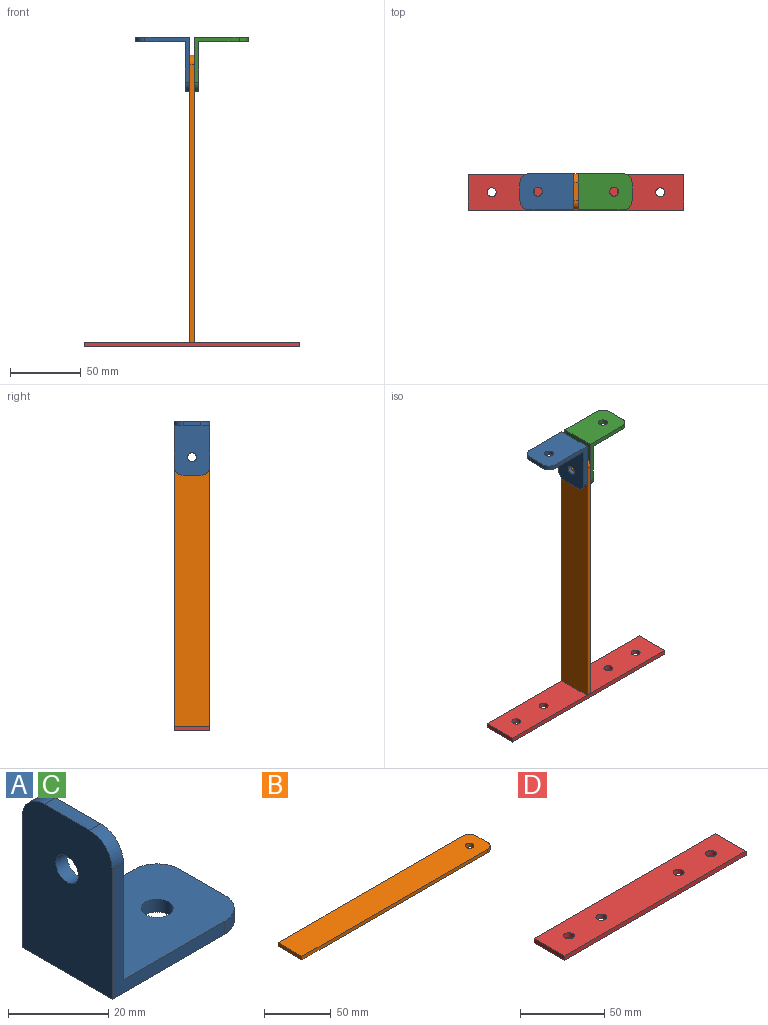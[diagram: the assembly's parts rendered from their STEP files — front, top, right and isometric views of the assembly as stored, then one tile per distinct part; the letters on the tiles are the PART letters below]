
ASSEMBLY  parts=4 mates=3
PART A: 14 faces, bbox 38.1x25.4x38.1 mm
  f0: plane 31.75x31.75mm, normal (0,-1,0), area 191.5mm2, adj f3,f5,f6,f7,f8,f11
  f1: plane 12.7x3.18mm, normal (1,0,0), area 40.3mm2, adj f5,f7,f8,f9
  f2: plane 31.75x31.75mm, normal (0,1,0), area 191.5mm2, adj f3,f5,f6,f7,f9,f10
  f3: plane 38.1x25.4mm, normal (-1,0,0), area 918.8mm2, adj f0,f2,f4,f5,f10,f11,f12
  f4: plane 12.7x3.18mm, normal (0,0,1), area 40.3mm2, adj f3,f6,f10,f11
  f5: plane 38.1x25.4mm, normal (0,0,-1), area 918.8mm2, adj f0,f1,f2,f3,f8,f9,f13
  f6: plane 34.93x25.4mm, normal (1,0,0), area 838.1mm2, adj f0,f2,f4,f7,f10,f11,f12
  f7: plane 34.93x25.4mm, normal (0,0,1), area 838.1mm2, adj f0,f1,f2,f6,f8,f9,f13
  f8: cylinder r=6.35mm len=6.35mm, axis (0,0,1), area 31.7mm2, adj f0,f1,f5,f7
  f9: cylinder r=6.35mm len=6.35mm, axis (0,0,-1), area 31.7mm2, adj f1,f2,f5,f7
  f10: cylinder r=6.35mm len=6.35mm, axis (1,0,0), area 31.7mm2, adj f2,f3,f4,f6
  f11: cylinder r=6.35mm len=6.35mm, axis (-1,0,0), area 31.7mm2, adj f0,f3,f4,f6
  f12: cylinder r=3.17mm len=6.35mm, axis (1,0,0), area 63.3mm2, adj f3,f6
  f13: cylinder r=3.17mm len=6.35mm, axis (0,0,1), area 63.3mm2, adj f5,f7
PART B: 9 faces, bbox 203.2x25.4x3.2 mm
  f0: plane 196.85x3.18mm, normal (0,1,0), area 625mm2, adj f1,f4,f5,f8
  f1: plane 25.4x3.18mm, normal (-1,0,0), area 80.6mm2, adj f0,f2,f4,f5
  f2: plane 196.85x3.18mm, normal (0,-1,0), area 625mm2, adj f1,f4,f5,f7
  f3: plane 12.7x3.18mm, normal (1,0,0), area 40.3mm2, adj f4,f5,f7,f8
  f4: plane 203.2x25.4mm, normal (0,0,1), area 5112.3mm2, adj f0,f1,f2,f3,f6,f7,f8
  f5: plane 203.2x25.4mm, normal (0,0,-1), area 5112.3mm2, adj f0,f1,f2,f3,f6,f7,f8
  f6: cylinder r=3.17mm len=6.35mm, axis (0,0,1), area 63.3mm2, adj f4,f5
  f7: cylinder r=6.35mm len=6.35mm, axis (0,0,1), area 31.7mm2, adj f2,f3,f4,f5
  f8: cylinder r=6.35mm len=6.35mm, axis (0,0,-1), area 31.7mm2, adj f0,f3,f4,f5
PART C: same geometry as A
PART D: 10 faces, bbox 152.4x25.4x3.2 mm
  f0: plane 152.4x25.4mm, normal (0,0,1), area 3744.3mm2, adj f2,f3,f4,f5,f6,f7,f8,f9
  f1: plane 152.4x25.4mm, normal (0,0,-1), area 3744.3mm2, adj f2,f3,f4,f5,f6,f7,f8,f9
  f2: plane 152.4x3.18mm, normal (0,1,0), area 483.9mm2, adj f0,f1,f3,f5
  f3: plane 25.4x3.18mm, normal (-1,0,0), area 80.6mm2, adj f0,f1,f2,f4
  f4: plane 152.4x3.18mm, normal (0,-1,0), area 483.9mm2, adj f0,f1,f3,f5
  f5: plane 25.4x3.18mm, normal (1,0,0), area 80.6mm2, adj f0,f1,f2,f4
  f6: cylinder r=3.17mm len=6.35mm, axis (0,0,1), area 63.3mm2, adj f0,f1
  f7: cylinder r=3.17mm len=6.35mm, axis (0,0,1), area 63.3mm2, adj f0,f1
  f8: cylinder r=3.17mm len=6.35mm, axis (0,0,1), area 63.3mm2, adj f0,f1
  f9: cylinder r=3.17mm len=6.35mm, axis (0,0,1), area 63.3mm2, adj f0,f1
PLACE A rot(axis=(0,1,0),180deg) t=(36.24,-79.37,232.66)mm
PLACE B rot(axis=(0,-1,0),90deg) t=(58.46,-74.39,118.36)mm
PLACE C rot(axis=(1,0,0),180deg) t=(77.51,-69.41,232.66)mm
PLACE D t=(56.88,-74.39,13.58)mm
MATE fastened A.f12 <-> B.f6  axis (1,0,0) through (55.29,-74.39,207.26)mm
MATE fastened C.f12 <-> B.f6  axis (-1,0,0) through (58.46,-74.39,207.26)mm
MATE fastened B.f1 <-> D.f0  axis (0,0,-1) through (56.88,-87.09,16.76)mm
